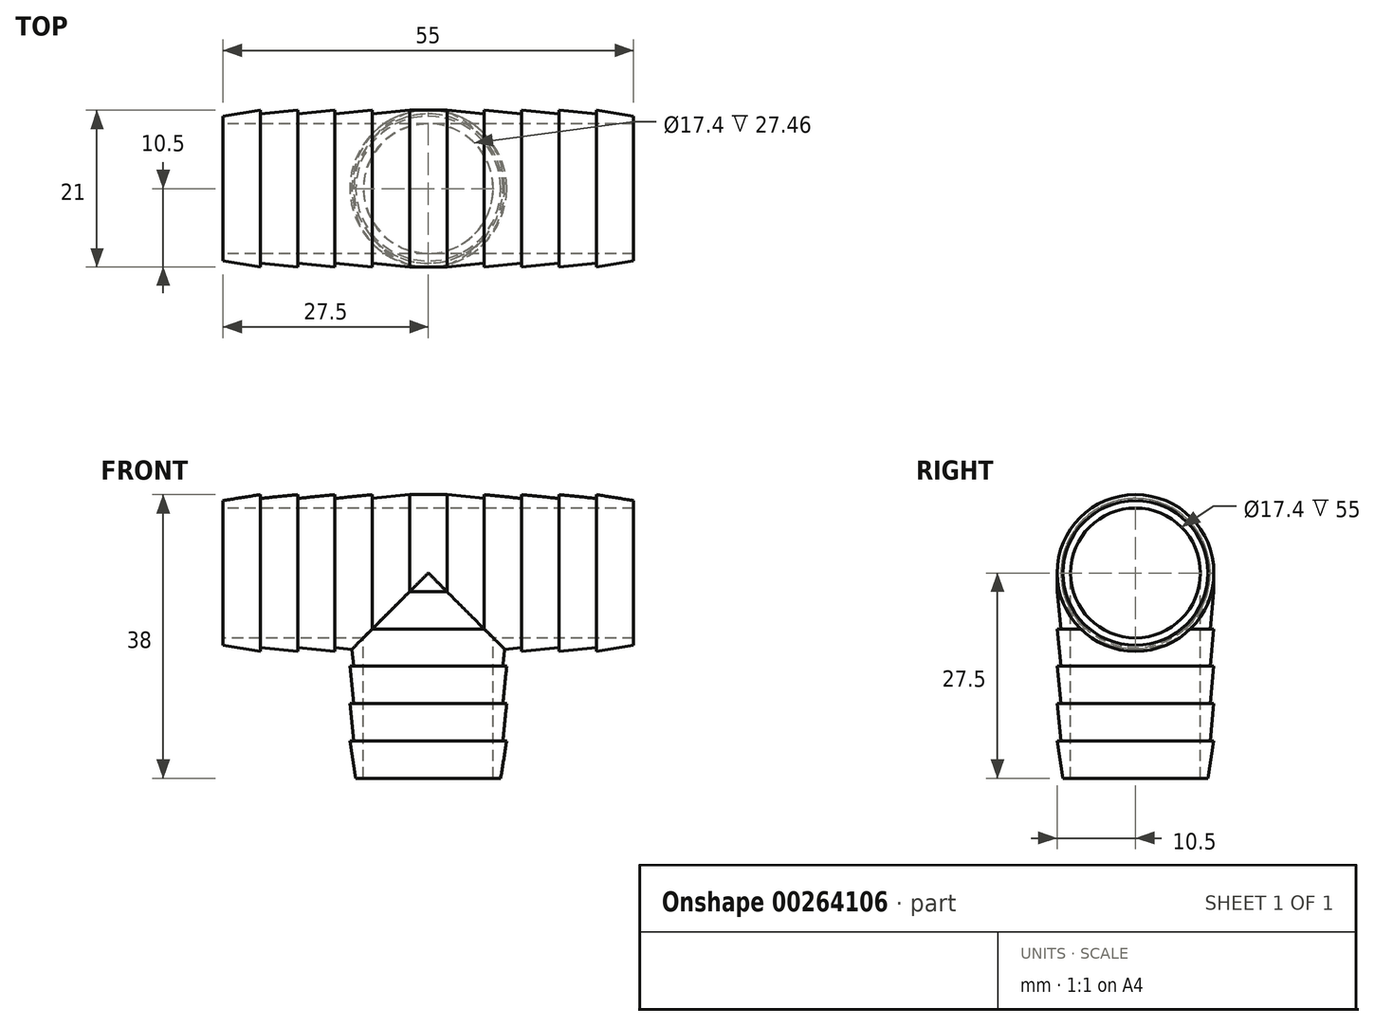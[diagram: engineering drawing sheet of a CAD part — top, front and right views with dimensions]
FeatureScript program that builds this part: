
annotation { "Feature Type Name" : "Feature", "Feature Type Description" : "" }
export const myFeature = defineFeature(function(context is Context, id is Id, definition is map)
    precondition{}
    {
        {
            var Q0;
            Q0=qCreatedBy(makeId("Top.planeOp"),FACE);
            var sketch = newSketch(context, id + "F0", { "sketchPlane" : qUnion([Q0])});
            skLineSegment(sketch, "E0", {"start": v(0, 0) * mm, "end": v(40.68, 0) * mm, "construction": true});
            skLineSegment(sketch, "E1", {"start": v(0, 0) * mm, "end": v(0, 20.7) * mm, "construction": true});
            skLineSegment(sketch, "E2", {"start": v(0, 8.7) * mm, "end": v(27.5, 8.7) * mm});
            skLineSegment(sketch, "E3", {"start": v(27.5, 8.7) * mm, "end": v(27.5, 9.7) * mm});
            skLineSegment(sketch, "E4", {"start": v(22.5, 8.18) * mm, "end": v(22.5, 10.5) * mm, "construction": true});
            skLineSegment(sketch, "E5", {"start": v(22.5, 10.5) * mm, "end": v(17.5, 10.5) * mm, "construction": true});
            skLineSegment(sketch, "E6", {"start": v(17.5, 10.5) * mm, "end": v(17.5, 7.93) * mm, "construction": true});
            skLineSegment(sketch, "E7", {"start": v(17.5, 7.93) * mm, "end": v(12.5, 7.93) * mm, "construction": true});
            skLineSegment(sketch, "E8", {"start": v(12.5, 7.93) * mm, "end": v(12.5, 10.5) * mm, "construction": true});
            skLineSegment(sketch, "E9", {"start": v(12.5, 10.5) * mm, "end": v(7.5, 10.5) * mm, "construction": true});
            skLineSegment(sketch, "E10", {"start": v(7.5, 10.5) * mm, "end": v(7.5, 7.93) * mm, "construction": true});
            skLineSegment(sketch, "E11", {"start": v(7.5, 7.93) * mm, "end": v(2.5, 7.93) * mm, "construction": true});
            skLineSegment(sketch, "E12", {"start": v(2.5, 7.93) * mm, "end": v(2.5, 10.5) * mm, "construction": true});
            skLineSegment(sketch, "E13", {"start": v(27.5, 9.7) * mm, "end": v(22.5, 10.5) * mm});
            skLineSegment(sketch, "E14", {"start": v(22.5, 10.5) * mm, "end": v(22.5, 10) * mm});
            skLineSegment(sketch, "E15", {"start": v(17.5, 10.5) * mm, "end": v(17.5, 10) * mm});
            skLineSegment(sketch, "E16", {"start": v(17.5, 10) * mm, "end": v(12.5, 10.5) * mm});
            skLineSegment(sketch, "E17", {"start": v(12.5, 10.5) * mm, "end": v(12.5, 10) * mm});
            skLineSegment(sketch, "E18", {"start": v(12.5, 10) * mm, "end": v(7.5, 10.5) * mm});
            skLineSegment(sketch, "E19", {"start": v(7.5, 10.5) * mm, "end": v(7.5, 10) * mm});
            skLineSegment(sketch, "E20", {"start": v(7.5, 10) * mm, "end": v(2.5, 10.5) * mm});
            skLineSegment(sketch, "E21", {"start": v(0, 10.5) * mm, "end": v(2.5, 10.5) * mm});
            skLineSegment(sketch, "E22", {"start": v(22.5, 10) * mm, "end": v(17.5, 10.5) * mm});
            skLineSegment(sketch, "E23", {"start": v(0, 10.5) * mm, "end": v(0, 8.7) * mm});
            skSolve(sketch);
        }
        {
            var Q0;
            Q0=makeQuery(id+"F0.imprint","IMPRINT",FACE,{"disambiguationData":[TD([[makeQuery(id+"F0.imprint","IMPRINT",EDGE,{"derivedFrom":sQuery(id+"F0.wireOp",EDGE,"E2")}),1.0]])]});
            var Q1;
            Q1=sQuery(id+"F0.wireOp",EDGE,"E0");
            revolve(context, id + "F1", {"entities" : qUnion([Q0]), "axis" : qUnion([Q1]), "revolveType" : RevolveType.FULL});
        }
        {
            var Q0;
            Q0=makeQuery(id+"F1.opRevolve","SWEPT_BODY",BODY,{"disambiguationData":[OSD([sQuery(id+"F0.wireOp",EDGE,"E2"),sQuery(id+"F0.wireOp",EDGE,"E3"),sQuery(id+"F0.wireOp",EDGE,"E13"),sQuery(id+"F0.wireOp",EDGE,"E14"),sQuery(id+"F0.wireOp",EDGE,"E15"),sQuery(id+"F0.wireOp",EDGE,"E16"),sQuery(id+"F0.wireOp",EDGE,"E17"),sQuery(id+"F0.wireOp",EDGE,"E18"),sQuery(id+"F0.wireOp",EDGE,"E19"),sQuery(id+"F0.wireOp",EDGE,"E20"),sQuery(id+"F0.wireOp",EDGE,"E21"),sQuery(id+"F0.wireOp",EDGE,"E22"),sQuery(id+"F0.wireOp",EDGE,"E23")])]});
            var Q1;
            Q1=sQuery(id+"F0.wireOp",EDGE,"E1");
            transform(context, id + "F2", {"entities" : qUnion([Q0]), "transformType" : TransformType.ROTATION, "transformAxis" : qUnion([Q1]), "angle" : 90 * degree, "makeCopy" : true});
        }
        {
            var Q0;
            Q0=makeQuery(id+"F1.opRevolve","SWEPT_BODY",BODY,{"disambiguationData":[OSD([sQuery(id+"F0.wireOp",EDGE,"E2"),sQuery(id+"F0.wireOp",EDGE,"E3"),sQuery(id+"F0.wireOp",EDGE,"E13"),sQuery(id+"F0.wireOp",EDGE,"E14"),sQuery(id+"F0.wireOp",EDGE,"E15"),sQuery(id+"F0.wireOp",EDGE,"E16"),sQuery(id+"F0.wireOp",EDGE,"E17"),sQuery(id+"F0.wireOp",EDGE,"E18"),sQuery(id+"F0.wireOp",EDGE,"E19"),sQuery(id+"F0.wireOp",EDGE,"E20"),sQuery(id+"F0.wireOp",EDGE,"E21"),sQuery(id+"F0.wireOp",EDGE,"E22"),sQuery(id+"F0.wireOp",EDGE,"E23")])]});
            var Q1;
            Q1=qCreatedBy(makeId("Right.planeOp"),FACE);
            mirror(context, id + "F3", {"operationType" : NewBodyOperationType.ADD, "entities" : qUnion([Q0]), "mirrorPlane" : qUnion([Q1])});
        }
        {
            var Q0;
            Q0=makeQuery(id+"F2.opPattern","COPY",FACE,{"derivedFrom":makeQuery(id+"F1.opRevolve","SWEPT_FACE",FACE,{"disambiguationData":[OSD([sQuery(id+"F0.wireOp",EDGE,"E3")])]}),"instanceName":"1"});
            var sketch = newSketch(context, id + "F4", { "sketchPlane" : qUnion([Q0])});
            skCircle(sketch, "E24.0", {"center": v(0, 0) * mm, "radius": 8.7 * mm});
            skSolve(sketch);
        }
        {
            var Q0;
            Q0=makeQuery(id+"F4.imprint","IMPRINT",FACE,{"disambiguationData":[TD([[makeQuery(id+"F4.imprint","IMPRINT",EDGE,{"derivedFrom":sQuery(id+"F4.wireOp",EDGE,"E24.0")}),-1.0]])]});
            extrude(context, id + "F5", {"entities" : qUnion([Q0]), "operationType" : NewBodyOperationType.REMOVE, "oppositeDirection" : true, "depth" : 27.46 * mm});
        }
        {
            var Q0;
            Q0=makeQuery(id+"F1.opRevolve","SWEPT_FACE",FACE,{"disambiguationData":[OSD([sQuery(id+"F0.wireOp",EDGE,"E3")])]});
            var sketch = newSketch(context, id + "F6", { "sketchPlane" : qUnion([Q0])});
            skCircle(sketch, "E25.0", {"center": v(0, 0) * mm, "radius": 8.7 * mm});
            skSolve(sketch);
        }
        {
            var Q0;
            Q0=makeQuery(id+"F6.imprint","IMPRINT",FACE,{"disambiguationData":[TD([[makeQuery(id+"F6.imprint","IMPRINT",EDGE,{"derivedFrom":sQuery(id+"F6.wireOp",EDGE,"E25.0")}),-1.0]])]});
            extrude(context, id + "F7", {"entities" : qUnion([Q0]), "operationType" : NewBodyOperationType.REMOVE, "endBound" : BoundingType.THROUGH_ALL, "oppositeDirection" : true, "depth" : 25 * mm});
        }
    });
